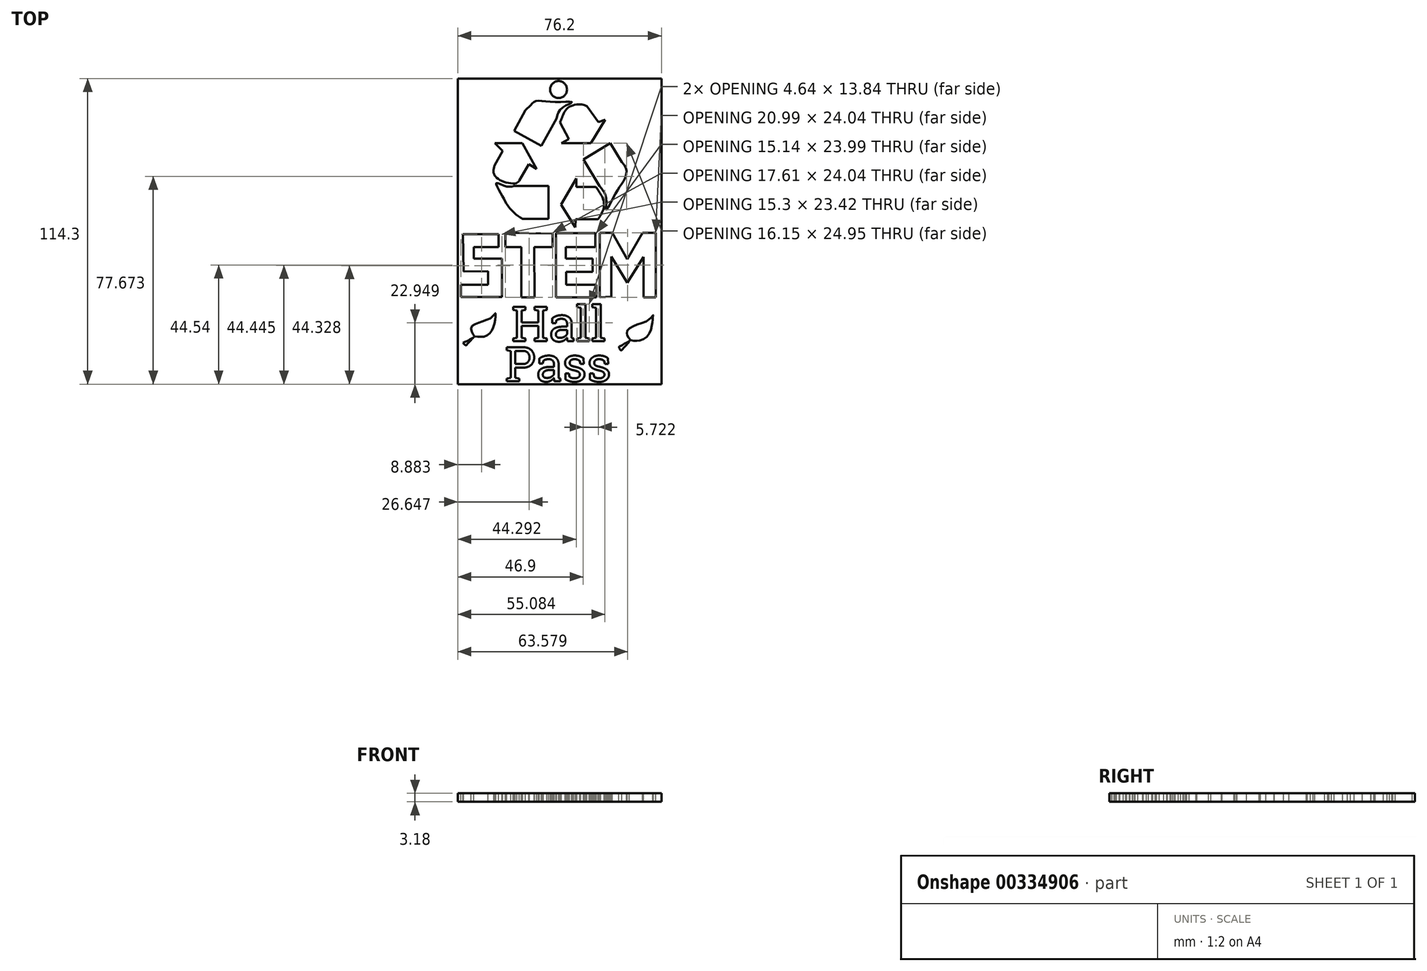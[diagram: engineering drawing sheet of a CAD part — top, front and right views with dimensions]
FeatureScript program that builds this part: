
annotation { "Feature Type Name" : "Feature", "Feature Type Description" : "" }
export const myFeature = defineFeature(function(context is Context, id is Id, definition is map)
    precondition{}
    {
        {
            var Q0;
            Q0=qCreatedBy(makeId("Top.planeOp"),FACE);
            var sketch = newSketch(context, id + "F0", { "sketchPlane" : qUnion([Q0])});
            skLineSegment(sketch, "E0.bottom", {"start": v(-42.7, 63) * mm, "end": v(33.5, 63) * mm});
            skLineSegment(sketch, "E0.top", {"start": v(-42.7, -51.3) * mm, "end": v(33.5, -51.3) * mm});
            skLineSegment(sketch, "E0.left", {"start": v(-42.7, 63) * mm, "end": v(-42.7, -51.3) * mm});
            skLineSegment(sketch, "E0.right", {"start": v(33.5, 63) * mm, "end": v(33.5, -51.3) * mm});
            skSolve(sketch);
        }
        {
            var Q0;
            Q0 = qSketchRegion(id + "F0", true);
            extrude(context, id + "F1", {"entities" : qUnion([Q0]), "depth" : 3.17 * mm});
        }
        {
            var Q0;
            Q0=makeQuery(id+"F1.opExtrude","CAP_FACE",FACE,{"disambiguationData":[OSD([sQuery(id+"F0.wireOp",EDGE,"E0.bottom"),sQuery(id+"F0.wireOp",EDGE,"E0.top"),sQuery(id+"F0.wireOp",EDGE,"E0.left"),sQuery(id+"F0.wireOp",EDGE,"E0.right")])],"isStart":false});
            var sketch = newSketch(context, id + "F2", { "sketchPlane" : qUnion([Q0])});
            skLineSegment(sketch, "E1", {"start": v(-5.98, 5.15) * mm, "end": v(-5.98, -18.84) * mm});
            skLineSegment(sketch, "E2", {"start": v(-5.98, -18.84) * mm, "end": v(9.16, -18.84) * mm});
            skLineSegment(sketch, "E3", {"start": v(9.16, -18.84) * mm, "end": v(9.16, -14.15) * mm});
            skLineSegment(sketch, "E4", {"start": v(9.16, -14.15) * mm, "end": v(-2.1, -14.15) * mm});
            skLineSegment(sketch, "E5", {"start": v(-2.1, -14.15) * mm, "end": v(-2.1, -9.33) * mm});
            skLineSegment(sketch, "E6", {"start": v(-2.1, -9.33) * mm, "end": v(7.8, -9.33) * mm});
            skLineSegment(sketch, "E7", {"start": v(7.8, -9.33) * mm, "end": v(7.8, -4.3) * mm});
            skLineSegment(sketch, "E8", {"start": v(7.8, -4.3) * mm, "end": v(-2.25, -4.3) * mm});
            skLineSegment(sketch, "E9", {"start": v(-2.25, -4.3) * mm, "end": v(-2.25, 0) * mm});
            skLineSegment(sketch, "E10", {"start": v(-2.25, 0) * mm, "end": v(8.76, 0) * mm});
            skLineSegment(sketch, "E11", {"start": v(8.76, 0) * mm, "end": v(8.76, 5.15) * mm});
            skLineSegment(sketch, "E12", {"start": v(8.76, 5.15) * mm, "end": v(-5.98, 5.15) * mm});
            skPoint(sketch, "E13.0.internal.orphan", {"position": v(-24.45, 0) * mm});
            skPoint(sketch, "E13.10.internal.orphan", {"position": v(-12.25, 0) * mm});
            skPoint(sketch, "E13.11.internal.orphan", {"position": v(-14.05, 0) * mm});
            skPoint(sketch, "E13.29.internal.orphan", {"position": v(-18.9, 0) * mm});
            skPoint(sketch, "E13.30.internal.orphan", {"position": v(-21.24, 0) * mm});
            skPoint(sketch, "E13.31.internal.orphan", {"position": v(-23.27, 0) * mm});
            skPoint(sketch, "E13.6.internal.orphan", {"position": v(-7.64, 5.15) * mm});
            skPoint(sketch, "E13.7.internal.orphan", {"position": v(-7.25, 0) * mm});
            skPoint(sketch, "E13.8.internal.orphan", {"position": v(-8.65, 0) * mm});
            skPoint(sketch, "E13.9.internal.orphan", {"position": v(-10.37, 0) * mm});
            skLineSegment(sketch, "E14", {"start": v(-24.86, 5.27) * mm, "end": v(-24.86, 0) * mm});
            skLineSegment(sketch, "E15", {"start": v(-24.86, 0) * mm, "end": v(-18.9, 0) * mm});
            skLineSegment(sketch, "E16", {"start": v(-18.9, 0) * mm, "end": v(-18.9, -18.77) * mm});
            skLineSegment(sketch, "E17", {"start": v(-18.9, -18.77) * mm, "end": v(-13.93, -18.77) * mm});
            skLineSegment(sketch, "E18", {"start": v(-13.93, -18.77) * mm, "end": v(-14.05, 0) * mm});
            skLineSegment(sketch, "E19", {"start": v(-7.25, 0) * mm, "end": v(-7.25, 5.07) * mm});
            skLineSegment(sketch, "E20", {"start": v(-7.25, 5.07) * mm, "end": v(-24.86, 5.27) * mm});
            skLineSegment(sketch, "E21", {"start": v(10.39, -18.77) * mm, "end": v(10.39, 5.27) * mm});
            skLineSegment(sketch, "E22", {"start": v(10.39, 5.27) * mm, "end": v(15.07, 5.27) * mm});
            skLineSegment(sketch, "E23", {"start": v(15.07, 5.27) * mm, "end": v(20.64, -4.64) * mm});
            skLineSegment(sketch, "E24", {"start": v(20.64, -4.64) * mm, "end": v(26.41, 5.27) * mm});
            skLineSegment(sketch, "E25", {"start": v(26.41, 5.27) * mm, "end": v(31.37, 5.27) * mm});
            skLineSegment(sketch, "E26", {"start": v(31.37, 5.27) * mm, "end": v(31.37, -18.77) * mm});
            skLineSegment(sketch, "E27", {"start": v(31.37, -18.77) * mm, "end": v(26.75, -18.77) * mm});
            skLineSegment(sketch, "E28", {"start": v(26.75, -18.77) * mm, "end": v(26.75, -3.7) * mm});
            skLineSegment(sketch, "E29", {"start": v(26.75, -3.7) * mm, "end": v(20.7, -13.34) * mm});
            skLineSegment(sketch, "E30", {"start": v(20.7, -13.34) * mm, "end": v(14.8, -3.56) * mm});
            skLineSegment(sketch, "E31", {"start": v(14.8, -3.56) * mm, "end": v(14.8, -18.57) * mm});
            skLineSegment(sketch, "E32", {"start": v(14.8, -18.57) * mm, "end": v(10.39, -18.77) * mm});
            skLineSegment(sketch, "E33", {"start": v(-14.05, 0) * mm, "end": v(-7.25, 0) * mm});
            skPoint(sketch, "E34.34.internal.orphan", {"position": v(-36.17, 0) * mm});
            skPoint(sketch, "E34.36.internal.orphan", {"position": v(-30.62, 0) * mm});
            skLineSegment(sketch, "E35", {"start": v(-27.46, 0) * mm, "end": v(-27.46, 4.75) * mm});
            skLineSegment(sketch, "E36", {"start": v(-27.46, 4.75) * mm, "end": v(-40.7, 4.75) * mm});
            skLineSegment(sketch, "E37", {"start": v(-31.34, -14.15) * mm, "end": v(-40.22, -14.15) * mm});
            skLineSegment(sketch, "E38", {"start": v(-40.22, -18.67) * mm, "end": v(-26.17, -18.67) * mm});
            skLineSegment(sketch, "E39", {"start": v(-26.17, -18.67) * mm, "end": v(-26.17, -4.3) * mm});
            skLineSegment(sketch, "E40", {"start": v(-26.17, -4.3) * mm, "end": v(-36.67, -4.3) * mm});
            skLineSegment(sketch, "E41", {"start": v(-36.67, -4.3) * mm, "end": v(-36.67, 0) * mm});
            skLineSegment(sketch, "E42", {"start": v(-36.67, 0) * mm, "end": v(-27.46, 0) * mm});
            skLineSegment(sketch, "E43", {"start": v(-31.34, -14.15) * mm, "end": v(-31.37, -9.07) * mm});
            skLineSegment(sketch, "E44", {"start": v(-31.37, -9.07) * mm, "end": v(-40.57, -9.12) * mm});
            skLineSegment(sketch, "E45", {"start": v(-40.57, -9.12) * mm, "end": v(-40.7, 4.75) * mm});
            skLineSegment(sketch, "E46", {"start": v(-40.22, -14.15) * mm, "end": v(-41.47, -14.15) * mm});
            skLineSegment(sketch, "E47", {"start": v(-41.47, -14.15) * mm, "end": v(-41.47, -18.67) * mm});
            skLineSegment(sketch, "E48", {"start": v(-41.47, -18.67) * mm, "end": v(-40.22, -18.67) * mm});
            skSolve(sketch);
        }
        {
            var Q0;
            Q0 = qSketchRegion(id + "F2", true);
            extrude(context, id + "F3", {"entities" : qUnion([Q0]), "operationType" : NewBodyOperationType.REMOVE, "oppositeDirection" : true, "depth" : 3.17 * mm});
        }
        {
            var Q0;
            Q0=makeQuery(id+"F1.opExtrude","CAP_FACE",FACE,{"disambiguationData":[OSD([sQuery(id+"F0.wireOp",EDGE,"E0.bottom"),sQuery(id+"F0.wireOp",EDGE,"E0.top"),sQuery(id+"F0.wireOp",EDGE,"E0.left"),sQuery(id+"F0.wireOp",EDGE,"E0.right")])],"isStart":false});
            var sketch = newSketch(context, id + "F4", { "sketchPlane" : qUnion([Q0])});
            skText(sketch, "E49", { "text": "Hall", "fontName": "RobotoSlab-Regular.ttf"});
            skText(sketch, "E50", { "text": "Pass\n", "fontName": "RobotoSlab-Regular.ttf"});
            const initialGuessF4  = {"E49": [-0.02263, -0.03526, 1, 0, 0.01308], "E50": [-0.02494, -0.05026, 1, 0, 0.01295]};
            skSetInitialGuess(sketch, initialGuessF4);
            skSolve(sketch);
        }
        {
            var Q0;
            Q0 = qSketchRegion(id + "F4", true);
            extrude(context, id + "F5", {"entities" : qUnion([Q0]), "operationType" : NewBodyOperationType.REMOVE, "oppositeDirection" : true, "depth" : 3.17 * mm});
        }
        {
            var Q0;
            {var subQ0=sQuery(id+"F0.wireOp",EDGE,"E0.bottom");var subQ1=sQuery(id+"F0.wireOp",EDGE,"E0.right");var subQ2=sQuery(id+"F0.wireOp",EDGE,"E0.top");var subQ3=sQuery(id+"F0.wireOp",EDGE,"E0.left");Q0=makeQuery(id+"F5.boolean.opBoolean","SPLIT",FACE,{"disambiguationData":[TD([makeQuery(id+"F1.opExtrude","SWEPT_FACE",FACE,{"disambiguationData":[OSD([subQ0])]})])],"derivedFrom":makeQuery(id+"F1.opExtrude","CAP_FACE",FACE,{"disambiguationData":[OSD([subQ0,subQ2,subQ3,subQ1])],"isStart":false})});}
            var sketch = newSketch(context, id + "F6", { "sketchPlane" : qUnion([Q0])});
            skFitSpline(sketch, "E51", {"points": [v(17.6, -37.34) * mm, v(18.42, -36.92) * mm, v(19.72, -36.14) * mm, v(20.63, -35.65) * mm, v(21.47, -35.2) * mm, v(21.05, -35.93) * mm, v(19.96, -37.13) * mm, v(18.98, -38.18) * mm, v(18.35, -38.7) * mm, v(18.06, -38.32) * mm, v(17.6, -37.34) * mm]});
            skFitSpline(sketch, "E52", {"points": [v(21.93, -34.84) * mm, v(21.05, -33.61) * mm, v(20.7, -32.98) * mm, v(20.53, -32.17) * mm, v(20.88, -31.01) * mm, v(22.63, -29.78) * mm, v(25.23, -28.76) * mm, v(28.75, -27.29) * mm, v(30.44, -25.53) * mm, v(30.26, -26.16) * mm, v(30.23, -27.25) * mm, v(30.05, -28.62) * mm, v(29.63, -30.55) * mm, v(28.71, -32.73) * mm, v(26.85, -34.46) * mm, v(24.7, -35.02) * mm, v(23.48, -35.02) * mm, v(21.93, -34.84) * mm]});
            skFitSpline(sketch, "E53", {"points": [v(-40.76, -35.87) * mm, v(-39.36, -35.3) * mm, v(-37.58, -34.2) * mm, v(-36.76, -33.85) * mm, v(-36.96, -33.99) * mm, v(-37.88, -35.03) * mm, v(-38.58, -35.76) * mm, v(-39.55, -36.7) * mm, v(-39.75, -36.74) * mm, v(-39.88, -36.69) * mm, v(-40.23, -36.28) * mm, v(-40.76, -35.87) * mm]});
            skFitSpline(sketch, "E54", {"points": [v(-36.4, -33.46) * mm, v(-36.96, -32.57) * mm, v(-37.65, -31.27) * mm, v(-37.58, -29.83) * mm, v(-36.05, -28.84) * mm, v(-34.22, -28.07) * mm, v(-31.16, -26.95) * mm, v(-29.6, -25.93) * mm, v(-28.48, -24.65) * mm, v(-28.5, -24.99) * mm, v(-28.62, -26.05) * mm, v(-28.84, -27.89) * mm, v(-29.48, -30.26) * mm, v(-30.37, -31.88) * mm, v(-31.71, -33.05) * mm, v(-33.36, -33.58) * mm, v(-34.84, -33.58) * mm, v(-36.4, -33.46) * mm]});
            skSolve(sketch);
        }
        {
            var Q0;
            Q0 = qSketchRegion(id + "F6", true);
            extrude(context, id + "F7", {"entities" : qUnion([Q0]), "operationType" : NewBodyOperationType.REMOVE, "oppositeDirection" : true, "depth" : 3.17 * mm});
        }
        {
            var Q0;
            {var subQ0=sQuery(id+"F0.wireOp",EDGE,"E0.bottom");var subQ1=sQuery(id+"F0.wireOp",EDGE,"E0.right");var subQ2=sQuery(id+"F0.wireOp",EDGE,"E0.top");var subQ3=sQuery(id+"F0.wireOp",EDGE,"E0.left");Q0=makeQuery(id+"F5.boolean.opBoolean","SPLIT",FACE,{"disambiguationData":[TD([makeQuery(id+"F1.opExtrude","SWEPT_FACE",FACE,{"disambiguationData":[OSD([subQ0])]})])],"derivedFrom":makeQuery(id+"F1.opExtrude","CAP_FACE",FACE,{"disambiguationData":[OSD([subQ0,subQ2,subQ3,subQ1])],"isStart":false})});}
            var sketch = newSketch(context, id + "F8", { "sketchPlane" : qUnion([Q0])});
            skPoint(sketch, "E55.secondSnap0", {"position": v(23.53, 0.31) * mm});
            skLineSegment(sketch, "E56", {"start": v(-29, 30.42) * mm, "end": v(-25.95, 35.94) * mm});
            skPoint(sketch, "E56.startSnap0", {"position": v(-30.3, 30.42) * mm});
            skLineSegment(sketch, "E57", {"start": v(-25.95, 35.94) * mm, "end": v(-28.86, 38.86) * mm});
            skLineSegment(sketch, "E58", {"start": v(-28.86, 38.86) * mm, "end": v(-18.51, 38.86) * mm});
            skLineSegment(sketch, "E59", {"start": v(-18.51, 38.86) * mm, "end": v(-13.2, 29.17) * mm});
            skLineSegment(sketch, "E60", {"start": v(-13.2, 29.17) * mm, "end": v(-16.13, 30.9) * mm});
            skLineSegment(sketch, "E61", {"start": v(-16.13, 30.9) * mm, "end": v(-19.66, 24.92) * mm});
            skLineSegment(sketch, "E62", {"start": v(-4.45, 46.55) * mm, "end": v(-1.13, 40.32) * mm});
            skLineSegment(sketch, "E63", {"start": v(-1.13, 40.32) * mm, "end": v(-3.91, 38.84) * mm});
            skLineSegment(sketch, "E64", {"start": v(-3.91, 38.84) * mm, "end": v(7.1, 38.84) * mm});
            skLineSegment(sketch, "E65", {"start": v(7.1, 38.84) * mm, "end": v(12.4, 47.62) * mm});
            skLineSegment(sketch, "E66", {"start": v(12.4, 47.62) * mm, "end": v(9.88, 46.69) * mm});
            skLineSegment(sketch, "E67", {"start": v(9.88, 46.69) * mm, "end": v(5.64, 52.66) * mm});
            skLineSegment(sketch, "E68", {"start": v(8.96, 22.4) * mm, "end": v(1.66, 22.4) * mm});
            skLineSegment(sketch, "E69", {"start": v(1.66, 22.4) * mm, "end": v(1.66, 25.59) * mm});
            skLineSegment(sketch, "E70", {"start": v(1.66, 25.59) * mm, "end": v(-4.05, 15.9) * mm});
            skLineSegment(sketch, "E71", {"start": v(-4.05, 15.9) * mm, "end": v(1.26, 7.27) * mm});
            skLineSegment(sketch, "E72", {"start": v(1.26, 7.27) * mm, "end": v(1.4, 10.33) * mm});
            skLineSegment(sketch, "E73", {"start": v(1.4, 10.33) * mm, "end": v(9.75, 10.33) * mm});
            skFitSpline(sketch, "E74", {"points": [v(8.96, 22.4) * mm, v(10.28, 20.54) * mm, v(11.87, 17.1) * mm, v(11.6, 13.64) * mm, v(9.75, 10.33) * mm], "startDerivative": vector(6.13, -8.07) * mm, "endDerivative": vector(-8.04, -12.1) * mm});
            skFitSpline(sketch, "E75", {"points": [v(-19.66, 24.92) * mm, v(-20.77, 23.86) * mm, v(-26.74, 24.92) * mm, v(-29.26, 27.71) * mm, v(-29, 30.42) * mm], "startDerivative": vector(-4.19, -7.56) * mm, "endDerivative": vector(3.08, 12.07) * mm});
            skFitSpline(sketch, "E76", {"points": [v(-4.45, 46.55) * mm, v(-3.52, 48.81) * mm, v(-1.53, 52) * mm, v(2.85, 53.32) * mm, v(5.64, 52.66) * mm], "startDerivative": vector(4.1, 9.9) * mm, "endDerivative": vector(10.92, -4.12) * mm});
            skLineSegment(sketch, "E77", {"start": v(-17.45, 51.2) * mm, "end": v(-21.57, 43.37) * mm});
            skLineSegment(sketch, "E78", {"start": v(-21.57, 43.37) * mm, "end": v(-11.48, 37.8) * mm});
            skLineSegment(sketch, "E79", {"start": v(-11.48, 37.8) * mm, "end": v(-5.77, 48.13) * mm});
            skLineSegment(sketch, "E80", {"start": v(4.31, 32.75) * mm, "end": v(14.4, 38.86) * mm});
            skLineSegment(sketch, "E81", {"start": v(14.4, 38.86) * mm, "end": v(18.7, 31.73) * mm});
            skLineSegment(sketch, "E82", {"start": v(4.31, 32.75) * mm, "end": v(10.36, 22.77) * mm});
            skLineSegment(sketch, "E83", {"start": v(-21.57, 22.77) * mm, "end": v(-8.7, 22.77) * mm});
            skLineSegment(sketch, "E84", {"start": v(-8.7, 22.77) * mm, "end": v(-8.7, 10.46) * mm});
            skLineSegment(sketch, "E85", {"start": v(-8.7, 10.46) * mm, "end": v(-18.38, 10.46) * mm});
            skFitSpline(sketch, "E86", {"points": [v(-21.57, 22.77) * mm, v(-25.02, 22.77) * mm, v(-28.33, 23.86) * mm, v(-26.48, 19.88) * mm, v(-24.35, 16.03) * mm, v(-21.57, 12.72) * mm, v(-18.38, 10.46) * mm], "startDerivative": vector(-20.37, -3.89) * mm, "endDerivative": vector(19.75, -12.28) * mm});
            skFitSpline(sketch, "E87", {"points": [v(10.36, 22.77) * mm, v(12, 20.54) * mm, v(12.94, 17.1) * mm, v(12.8, 13.9) * mm, v(15.99, 19.35) * mm, v(18.78, 23.86) * mm, v(20.5, 28.24) * mm, v(18.7, 31.73) * mm], "startDerivative": vector(15.15, -18.17) * mm, "endDerivative": vector(-18.8, 23.87) * mm});
            skFitSpline(sketch, "E88", {"points": [v(-17.45, 51.2) * mm, v(-15.33, 53.06) * mm, v(-13.6, 54.52) * mm, v(-7.23, 54.25) * mm, v(0, 54.12) * mm, v(-3.65, 52) * mm, v(-5.77, 48.13) * mm], "startDerivative": vector(16.96, 13.54) * mm, "endDerivative": vector(-6.6, -24.96) * mm});
            skSolve(sketch);
        }
        {
            var Q0;
            Q0 = qSketchRegion(id + "F8", true);
            extrude(context, id + "F9", {"entities" : qUnion([Q0]), "operationType" : NewBodyOperationType.REMOVE, "oppositeDirection" : true, "depth" : 3.17 * mm});
        }
        {
            var Q0;
            {var subQ0=sQuery(id+"F0.wireOp",EDGE,"E0.bottom");var subQ1=sQuery(id+"F0.wireOp",EDGE,"E0.right");var subQ2=sQuery(id+"F0.wireOp",EDGE,"E0.top");var subQ3=sQuery(id+"F0.wireOp",EDGE,"E0.left");Q0=makeQuery(id+"F5.boolean.opBoolean","SPLIT",FACE,{"disambiguationData":[TD([makeQuery(id+"F1.opExtrude","SWEPT_FACE",FACE,{"disambiguationData":[OSD([subQ0])]})])],"derivedFrom":makeQuery(id+"F1.opExtrude","CAP_FACE",FACE,{"disambiguationData":[OSD([subQ0,subQ2,subQ3,subQ1])],"isStart":false})});}
            var sketch = newSketch(context, id + "F10", { "sketchPlane" : qUnion([Q0])});
            skCircle(sketch, "E89", {"center": v(-5, 58.85) * mm, "radius": 3.18 * mm});
            skSolve(sketch);
        }
        {
            var Q0;
            Q0 = qSketchRegion(id + "F10", true);
            extrude(context, id + "F11", {"entities" : qUnion([Q0]), "operationType" : NewBodyOperationType.REMOVE, "oppositeDirection" : true, "depth" : 3.17 * mm});
        }
    });
